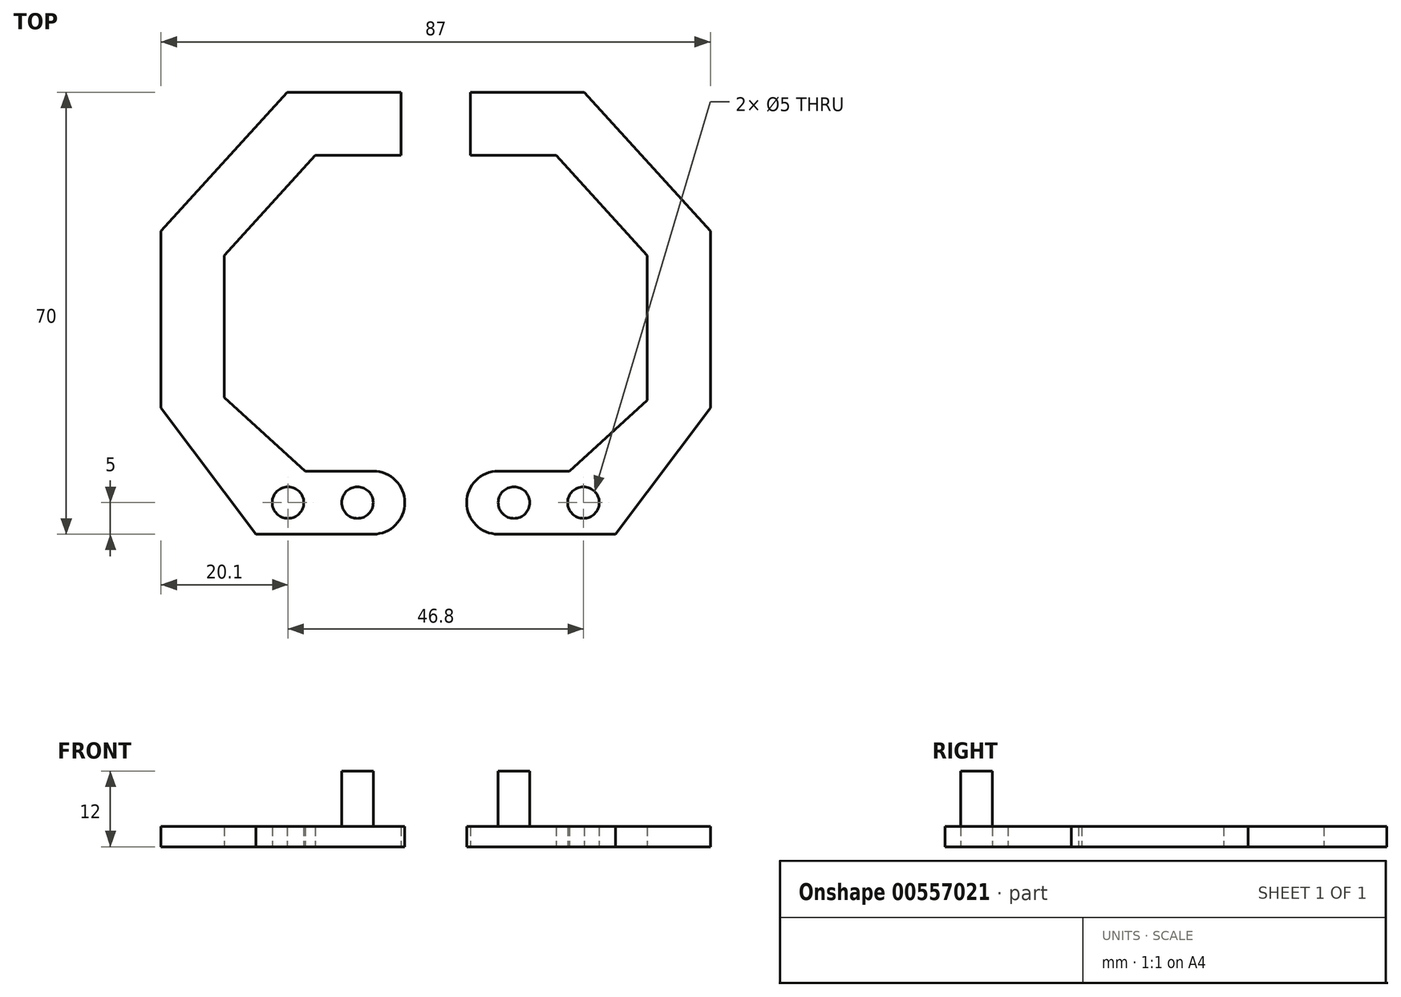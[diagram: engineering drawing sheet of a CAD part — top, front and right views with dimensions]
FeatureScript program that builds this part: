
annotation { "Feature Type Name" : "Feature", "Feature Type Description" : "" }
export const myFeature = defineFeature(function(context is Context, id is Id, definition is map)
    precondition{}
    {
        {
            var Q0;
            Q0=qCreatedBy(makeId("Top.planeOp"),FACE);
            var sketch = newSketch(context, id + "F0", { "sketchPlane" : qUnion([Q0])});
            skLineSegment(sketch, "E0.bottom", {"start": v(43.5, -35) * mm, "end": v(-43.5, -35) * mm});
            skLineSegment(sketch, "E0.top", {"start": v(43.5, 35) * mm, "end": v(-43.5, 35) * mm});
            skLineSegment(sketch, "E0.left", {"start": v(43.5, -35) * mm, "end": v(43.5, 35) * mm});
            skLineSegment(sketch, "E0.right", {"start": v(-43.5, -35) * mm, "end": v(-43.5, 35) * mm});
            skPoint(sketch, "E0.middle", {"position": v(0, 0) * mm});
            skLineSegment(sketch, "E1", {"start": v(-43.5, -15) * mm, "end": v(-28.5, -35) * mm});
            skLineSegment(sketch, "E2", {"start": v(28.5, -35) * mm, "end": v(43.5, -15) * mm});
            skLineSegment(sketch, "E3", {"start": v(-43.5, 13) * mm, "end": v(-23.5, 35) * mm});
            skLineSegment(sketch, "E4", {"start": v(43.5, 13) * mm, "end": v(23.5, 35) * mm});
            skLineSegment(sketch, "E5", {"start": v(-23.5, 35) * mm, "end": v(-5.5, 35) * mm});
            skLineSegment(sketch, "E6", {"start": v(-5.5, 35) * mm, "end": v(-5.5, 25) * mm});
            skLineSegment(sketch, "E7", {"start": v(-5.5, 25) * mm, "end": v(-19.08, 25) * mm});
            skLineSegment(sketch, "E8", {"start": v(-19.08, 25) * mm, "end": v(-33.5, 9.13) * mm});
            skLineSegment(sketch, "E9", {"start": v(-33.5, 9.13) * mm, "end": v(-33.5, -13.36) * mm});
            skLineSegment(sketch, "E10", {"start": v(-33.5, -13.36) * mm, "end": v(-20.7, -25) * mm});
            skLineSegment(sketch, "E11", {"start": v(-20.7, -25) * mm, "end": v(-4.9, -25) * mm});
            skLineSegment(sketch, "E12", {"start": v(-4.9, -25) * mm, "end": v(-4.9, -35) * mm});
            skLineSegment(sketch, "E13", {"start": v(23.5, 35) * mm, "end": v(5.5, 35) * mm});
            skLineSegment(sketch, "E14", {"start": v(5.5, 35) * mm, "end": v(5.5, 25) * mm});
            skLineSegment(sketch, "E15", {"start": v(5.5, 25) * mm, "end": v(19.08, 25) * mm});
            skLineSegment(sketch, "E16", {"start": v(19.08, 25) * mm, "end": v(33.5, 9.13) * mm});
            skLineSegment(sketch, "E17", {"start": v(33.5, 9.13) * mm, "end": v(33.5, -13.82) * mm});
            skLineSegment(sketch, "E18", {"start": v(33.5, -13.82) * mm, "end": v(21.2, -25) * mm});
            skLineSegment(sketch, "E19", {"start": v(21.2, -25) * mm, "end": v(4.9, -25) * mm});
            skLineSegment(sketch, "E20", {"start": v(4.9, -25) * mm, "end": v(4.9, -35) * mm});
            skCircle(sketch, "E21", {"center": v(12.4, -30) * mm, "radius": 2.5 * mm});
            skCircle(sketch, "E22", {"center": v(-12.4, -30) * mm, "radius": 2.5 * mm});
            skCircle(sketch, "E23", {"center": v(23.4, -30) * mm, "radius": 2.5 * mm});
            skCircle(sketch, "E24", {"center": v(-23.4, -30) * mm, "radius": 2.5 * mm});
            skSolve(sketch);
        }
        {
            var Q0;
            {var subQ0=sQuery(id+"F0.wireOp",EDGE,"E2");Q0=makeQuery(id+"F0.imprint","IMPRINT",FACE,{"disambiguationData":[TD([[makeQuery(id+"F0.imprint","IMPRINT",EDGE,{"derivedFrom":subQ0}),1.0]])]});}
            var Q1;
            {var subQ0=sQuery(id+"F0.wireOp",EDGE,"E1");Q1=makeQuery(id+"F0.imprint","IMPRINT",FACE,{"disambiguationData":[TD([[makeQuery(id+"F0.imprint","IMPRINT",EDGE,{"derivedFrom":subQ0}),1.0]])]});}
            extrude(context, id + "F1", {"entities" : qUnion([Q0, Q1]), "depth" : 3.2 * mm});
        }
        {
            var Q0;
            Q0=makeQuery(id+"F0.imprint","IMPRINT",FACE,{"disambiguationData":[TD([[makeQuery(id+"F0.imprint","IMPRINT",EDGE,{"derivedFrom":sQuery(id+"F0.wireOp",EDGE,"E21")}),1.0]])]});
            extrude(context, id + "F2", {"entities" : qUnion([Q0]), "operationType" : NewBodyOperationType.ADD, "depth" : 12 * mm, "offsetDistance" : 25 * mm});
        }
        {
            var Q0;
            Q0=makeQuery(id+"F0.imprint","IMPRINT",FACE,{"disambiguationData":[TD([[makeQuery(id+"F0.imprint","IMPRINT",EDGE,{"derivedFrom":sQuery(id+"F0.wireOp",EDGE,"E22")}),1.0]])]});
            extrude(context, id + "F3", {"entities" : qUnion([Q0]), "operationType" : NewBodyOperationType.ADD, "depth" : 12 * mm, "offsetDistance" : 25 * mm});
        }
        {
            var Q0;
            Q0=makeQuery(id+"F1.opExtrude","SWEPT_EDGE",EDGE,{"disambiguationData":[OSD([sQuery(id+"F0.wireOp",EDGE,"E0.bottom"),sQuery(id+"F0.wireOp",EDGE,"E20")])]});
            var Q1;
            Q1=makeQuery(id+"F1.opExtrude","SWEPT_EDGE",EDGE,{"disambiguationData":[OSD([sQuery(id+"F0.wireOp",EDGE,"E19"),sQuery(id+"F0.wireOp",EDGE,"E20")])]});
            fillet(context, id + "F4", {"entities" : qUnion([Q0, Q1]), "radius" : 5 * mm, "tangentPropagation" : true, "allowEdgeOverflow" : false});
        }
        {
            var Q0;
            Q0=makeQuery(id+"F1.opExtrude","SWEPT_EDGE",EDGE,{"disambiguationData":[OSD([sQuery(id+"F0.wireOp",EDGE,"E0.bottom"),sQuery(id+"F0.wireOp",EDGE,"E12")])]});
            var Q1;
            Q1=makeQuery(id+"F1.opExtrude","SWEPT_EDGE",EDGE,{"disambiguationData":[OSD([sQuery(id+"F0.wireOp",EDGE,"E11"),sQuery(id+"F0.wireOp",EDGE,"E12")])]});
            fillet(context, id + "F5", {"entities" : qUnion([Q0, Q1]), "radius" : 5 * mm, "tangentPropagation" : true, "allowEdgeOverflow" : false});
        }
    });
